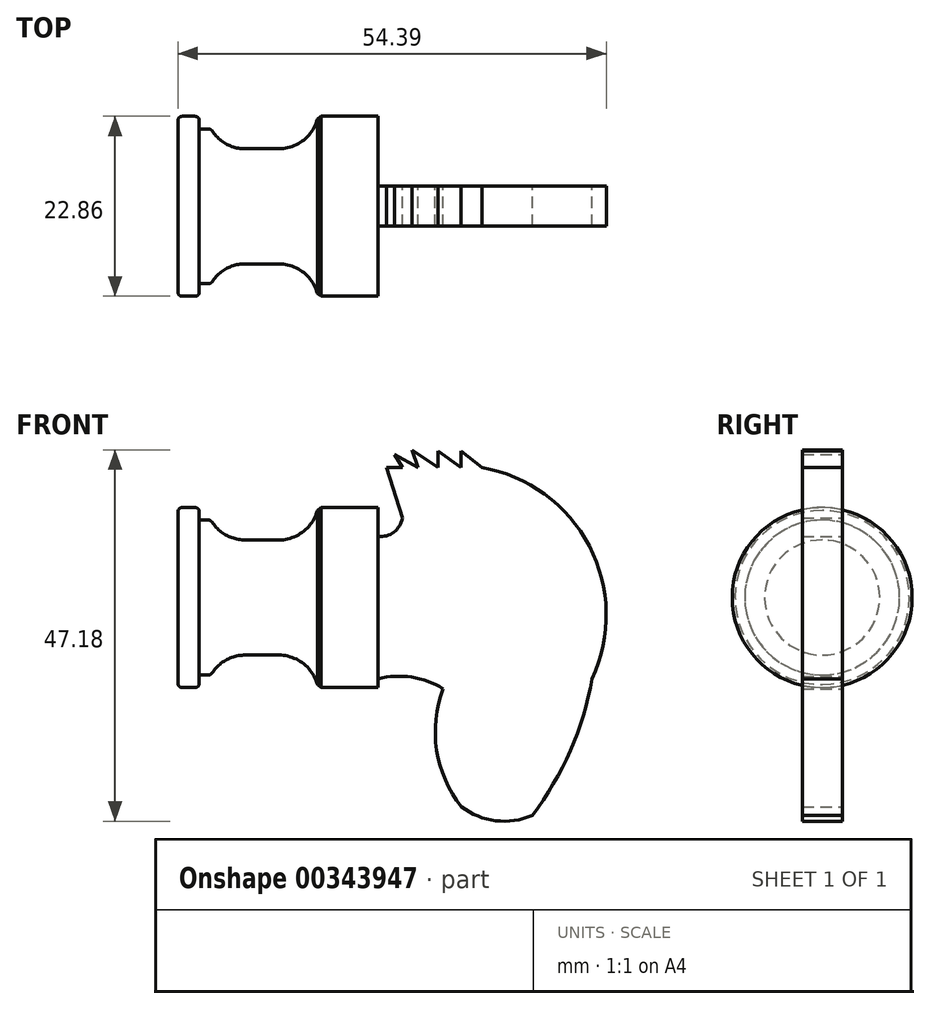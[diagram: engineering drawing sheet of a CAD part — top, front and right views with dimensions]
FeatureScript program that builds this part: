
annotation { "Feature Type Name" : "Feature", "Feature Type Description" : "" }
export const myFeature = defineFeature(function(context is Context, id is Id, definition is map)
    precondition{}
    {
        {
            var Q0;
            Q0=qCreatedBy(makeId("Front.planeOp"),FACE);
            var sketch = newSketch(context, id + "F0", { "sketchPlane" : qUnion([Q0])});
            skLineSegment(sketch, "E0", {"start": v(0, 0) * mm, "end": v(-25.4, 0) * mm});
            skLineSegment(sketch, "E1", {"start": v(-25.4, 0) * mm, "end": v(-25.4, 11.43) * mm});
            skLineSegment(sketch, "E2", {"start": v(-25.4, 11.43) * mm, "end": v(-22.71, 11.43) * mm});
            skLineSegment(sketch, "E3", {"start": v(-22.71, 11.43) * mm, "end": v(-22.71, 9.84) * mm});
            skLineSegment(sketch, "E4", {"start": v(-22.71, 9.84) * mm, "end": v(-21.25, 9.84) * mm});
            skLineSegment(sketch, "E5", {"start": v(-21.25, 9.84) * mm, "end": v(-20.32, 7.31) * mm});
            skLineSegment(sketch, "E6", {"start": v(-20.32, 7.31) * mm, "end": v(-7.62, 7.31) * mm});
            skLineSegment(sketch, "E7", {"start": v(-7.62, 7.31) * mm, "end": v(-7.62, 11.43) * mm});
            skLineSegment(sketch, "E8", {"start": v(-7.62, 11.43) * mm, "end": v(0, 11.43) * mm});
            skLineSegment(sketch, "E9", {"start": v(0, 11.43) * mm, "end": v(0, 0) * mm});
            skSolve(sketch);
        }
        {
            var Q0;
            Q0=makeQuery(id+"F0.imprint","IMPRINT",FACE,{"disambiguationData":[TD([[makeQuery(id+"F0.imprint","IMPRINT",EDGE,{"derivedFrom":sQuery(id+"F0.wireOp",EDGE,"E0")}),-1.0]])]});
            var Q1;
            Q1=sQuery(id+"F0.wireOp",EDGE,"E0");
            revolve(context, id + "F1", {"entities" : qUnion([Q0]), "axis" : qUnion([Q1]), "revolveType" : RevolveType.FULL});
        }
        {
            var Q0;
            Q0=makeQuery(id+"F1.opRevolve","SWEPT_EDGE",EDGE,{"disambiguationData":[OSD([sQuery(id+"F0.wireOp",EDGE,"E5"),sQuery(id+"F0.wireOp",EDGE,"E6")])]});
            fillet(context, id + "F2", {"entities" : qUnion([Q0]), "radius" : 5.08 * mm, "tangentPropagation" : true, "allowEdgeOverflow" : false});
        }
        {
            var Q0;
            Q0=makeQuery(id+"F1.opRevolve","SWEPT_EDGE",EDGE,{"disambiguationData":[OSD([sQuery(id+"F0.wireOp",EDGE,"E6"),sQuery(id+"F0.wireOp",EDGE,"E7")])]});
            fillet(context, id + "F3", {"entities" : qUnion([Q0]), "radius" : 5.08 * mm, "tangentPropagation" : true, "allowEdgeOverflow" : false});
        }
        {
            var Q0;
            Q0=makeQuery(id+"F2.opFillet","BLEND_EDGE",EDGE,{"blendedFrom":[makeQuery(id+"F1.opRevolve","SWEPT_EDGE",EDGE,{"disambiguationData":[OSD([sQuery(id+"F0.wireOp",EDGE,"E5"),sQuery(id+"F0.wireOp",EDGE,"E6")])]}),makeQuery(id+"F1.opRevolve","SWEPT_FACE",FACE,{"disambiguationData":[OSD([sQuery(id+"F0.wireOp",EDGE,"E4")])]})],"blendedInto":[makeQuery(id+"F1.opRevolve","SWEPT_FACE",FACE,{"disambiguationData":[OSD([sQuery(id+"F0.wireOp",EDGE,"E4")])]})]});
            var Q1;
            Q1=makeQuery(id+"F1.opRevolve","SWEPT_EDGE",EDGE,{"disambiguationData":[OSD([sQuery(id+"F0.wireOp",EDGE,"E2"),sQuery(id+"F0.wireOp",EDGE,"E3")])]});
            var Q2;
            Q2=makeQuery(id+"F1.opRevolve","SWEPT_EDGE",EDGE,{"disambiguationData":[OSD([sQuery(id+"F0.wireOp",EDGE,"E1"),sQuery(id+"F0.wireOp",EDGE,"E2")])]});
            fillet(context, id + "F4", {"entities" : qUnion([Q0, Q1, Q2]), "radius" : 0.5 * mm, "tangentPropagation" : true, "allowEdgeOverflow" : false});
        }
        {
            var Q0;
            {var subQ0=sQuery(id+"F0.wireOp",EDGE,"E9");var subQ1=sQuery(id+"F0.wireOp",EDGE,"E8");var subQ2=makeQuery(id+"F1.opRevolve","SWEPT_EDGE",EDGE,{"disambiguationData":[OSD([subQ1,subQ0])]});Q0=makeQuery(id+"F3.opFillet","BLEND_EDGE",EDGE,{"blendedFrom":[makeQuery(id+"F1.opRevolve","SWEPT_EDGE",EDGE,{"disambiguationData":[OSD([sQuery(id+"F0.wireOp",EDGE,"E6"),sQuery(id+"F0.wireOp",EDGE,"E7")])]}),makeQuery(id+"FKdUeLkxdvxAeGn_1.boolean.opBoolean","MERGE",FACE,{"derivedFrom":[makeQuery(id+"F1.opRevolve","SWEPT_FACE",FACE,{"disambiguationData":[OSD([subQ1])]}),makeQuery(id+"FKdUeLkxdvxAeGn_1.opExtrude","SWEPT_FACE",FACE,{"disambiguationData":[OSD([subQ1,subQ0]),TDD([makeQuery(id+"FhPrJ5y7E5olnpu_1.imprint","IMPRINT",EDGE,{"disambiguationData":[TD([[makeQuery(id+"FhPrJ5y7E5olnpu_1.imprint","INTERSECT",VERTEX,{"derivedFrom":[subQ2,sQuery(id+"FhPrJ5y7E5olnpu_1.wireOp",EDGE,"5swccAFu-Qq9y-H5FG-WLZN-0cyFNXjqbd3L")]}),1.0]])],"derivedFrom":subQ2})])]}),makeQuery(id+"FKdUeLkxdvxAeGn_1.opExtrude","SWEPT_FACE",FACE,{"disambiguationData":[OSD([subQ1,subQ0]),TDD([makeQuery(id+"FhPrJ5y7E5olnpu_1.imprint","IMPRINT",EDGE,{"disambiguationData":[TD([[makeQuery(id+"FhPrJ5y7E5olnpu_1.imprint","INTERSECT",VERTEX,{"derivedFrom":[subQ2,sQuery(id+"FhPrJ5y7E5olnpu_1.wireOp",EDGE,"yrlBlJsE-glzK-ckup-w4H4-O8etLDBYbZ2E")]}),1.0]])],"derivedFrom":subQ2})])]}),makeQuery(id+"FKdUeLkxdvxAeGn_1.opExtrude","SWEPT_FACE",FACE,{"disambiguationData":[OSD([subQ1,subQ0]),TDD([makeQuery(id+"FhPrJ5y7E5olnpu_1.imprint","IMPRINT",EDGE,{"disambiguationData":[TD([[makeQuery(id+"FhPrJ5y7E5olnpu_1.imprint","INTERSECT",VERTEX,{"derivedFrom":[subQ2,sQuery(id+"FhPrJ5y7E5olnpu_1.wireOp",EDGE,"59esLNOy-bGTi-q598-Dafd-GjDcgzXxW0rH")]}),-1.0]])],"derivedFrom":subQ2})])]}),makeQuery(id+"FKdUeLkxdvxAeGn_1.opExtrude","SWEPT_FACE",FACE,{"disambiguationData":[OSD([subQ1,subQ0]),TDD([makeQuery(id+"FhPrJ5y7E5olnpu_1.imprint","IMPRINT",EDGE,{"disambiguationData":[TD([[makeQuery(id+"FhPrJ5y7E5olnpu_1.imprint","INTERSECT",VERTEX,{"derivedFrom":[subQ2,sQuery(id+"FhPrJ5y7E5olnpu_1.wireOp",EDGE,"8v8Xe1NO-uW00-CEbA-Of9p-lGgIFj4n3XNv")]}),-1.0]])],"derivedFrom":subQ2})])]})]})],"blendedInto":[makeQuery(id+"FKdUeLkxdvxAeGn_1.boolean.opBoolean","MERGE",FACE,{"derivedFrom":[makeQuery(id+"F1.opRevolve","SWEPT_FACE",FACE,{"disambiguationData":[OSD([subQ1])]}),makeQuery(id+"FKdUeLkxdvxAeGn_1.opExtrude","SWEPT_FACE",FACE,{"disambiguationData":[OSD([subQ1,subQ0]),TDD([makeQuery(id+"FhPrJ5y7E5olnpu_1.imprint","IMPRINT",EDGE,{"disambiguationData":[TD([[makeQuery(id+"FhPrJ5y7E5olnpu_1.imprint","INTERSECT",VERTEX,{"derivedFrom":[subQ2,sQuery(id+"FhPrJ5y7E5olnpu_1.wireOp",EDGE,"5swccAFu-Qq9y-H5FG-WLZN-0cyFNXjqbd3L")]}),1.0]])],"derivedFrom":subQ2})])]}),makeQuery(id+"FKdUeLkxdvxAeGn_1.opExtrude","SWEPT_FACE",FACE,{"disambiguationData":[OSD([subQ1,subQ0]),TDD([makeQuery(id+"FhPrJ5y7E5olnpu_1.imprint","IMPRINT",EDGE,{"disambiguationData":[TD([[makeQuery(id+"FhPrJ5y7E5olnpu_1.imprint","INTERSECT",VERTEX,{"derivedFrom":[subQ2,sQuery(id+"FhPrJ5y7E5olnpu_1.wireOp",EDGE,"yrlBlJsE-glzK-ckup-w4H4-O8etLDBYbZ2E")]}),1.0]])],"derivedFrom":subQ2})])]}),makeQuery(id+"FKdUeLkxdvxAeGn_1.opExtrude","SWEPT_FACE",FACE,{"disambiguationData":[OSD([subQ1,subQ0]),TDD([makeQuery(id+"FhPrJ5y7E5olnpu_1.imprint","IMPRINT",EDGE,{"disambiguationData":[TD([[makeQuery(id+"FhPrJ5y7E5olnpu_1.imprint","INTERSECT",VERTEX,{"derivedFrom":[subQ2,sQuery(id+"FhPrJ5y7E5olnpu_1.wireOp",EDGE,"59esLNOy-bGTi-q598-Dafd-GjDcgzXxW0rH")]}),-1.0]])],"derivedFrom":subQ2})])]}),makeQuery(id+"FKdUeLkxdvxAeGn_1.opExtrude","SWEPT_FACE",FACE,{"disambiguationData":[OSD([subQ1,subQ0]),TDD([makeQuery(id+"FhPrJ5y7E5olnpu_1.imprint","IMPRINT",EDGE,{"disambiguationData":[TD([[makeQuery(id+"FhPrJ5y7E5olnpu_1.imprint","INTERSECT",VERTEX,{"derivedFrom":[subQ2,sQuery(id+"FhPrJ5y7E5olnpu_1.wireOp",EDGE,"8v8Xe1NO-uW00-CEbA-Of9p-lGgIFj4n3XNv")]}),-1.0]])],"derivedFrom":subQ2})])]})]})]});}
            chamfer(context, id + "F5", {"entities" : qUnion([Q0]), "width" : 0.5 * mm, "tangentPropagation" : true});
        }
        {
            var Q0;
            Q0=qCreatedBy(makeId("Front.planeOp"),FACE);
            var sketch = newSketch(context, id + "F6", { "sketchPlane" : qUnion([Q0])});
            skArc(sketch, "E10", {"start": v(0, 7.76) * mm, "mid": v(2, 8.32) * mm, "end": v(3.1, 10.1) * mm});
            skLineSegment(sketch, "E11", {"start": v(3.1, 10.1) * mm, "end": v(1.1, 16.51) * mm});
            skLineSegment(sketch, "E12", {"start": v(1.1, 16.51) * mm, "end": v(3.1, 16.51) * mm});
            skLineSegment(sketch, "E13", {"start": v(3.1, 16.51) * mm, "end": v(2.1, 18.18) * mm});
            skPoint(sketch, "E13.endSnap0", {"position": v(2.1, 16.51) * mm});
            skLineSegment(sketch, "E14", {"start": v(2.1, 18.18) * mm, "end": v(5.1, 16.51) * mm});
            skLineSegment(sketch, "E15", {"start": v(5.1, 16.51) * mm, "end": v(4.34, 18.77) * mm});
            skLineSegment(sketch, "E16", {"start": v(4.34, 18.77) * mm, "end": v(7.6, 16.51) * mm});
            skLineSegment(sketch, "E17", {"start": v(7.6, 16.51) * mm, "end": v(7.6, 18.6) * mm});
            skLineSegment(sketch, "E18", {"start": v(7.6, 18.6) * mm, "end": v(10.51, 16.51) * mm});
            skLineSegment(sketch, "E19", {"start": v(10.51, 16.51) * mm, "end": v(10.51, 18.6) * mm});
            skLineSegment(sketch, "E20", {"start": v(10.51, 18.6) * mm, "end": v(13.18, 16.51) * mm});
            skArc(sketch, "E21", {"start": v(27.19, -10.33) * mm, "mid": v(26.83, 6.56) * mm, "end": v(13.18, 16.51) * mm});
            skArc(sketch, "E22", {"start": v(19.6, -27.67) * mm, "mid": v(24.42, -19.45) * mm, "end": v(27.19, -10.33) * mm});
            skArc(sketch, "E23", {"start": v(10.6, -26.59) * mm, "mid": v(14.95, -28.35) * mm, "end": v(19.6, -27.67) * mm});
            skArc(sketch, "E24", {"start": v(8.26, -11.58) * mm, "mid": v(7.45, -19.4) * mm, "end": v(10.6, -26.59) * mm});
            skArc(sketch, "E25", {"start": v(8.26, -11.58) * mm, "mid": v(4.26, -10.12) * mm, "end": v(0, -10.33) * mm});
            skLineSegment(sketch, "E26", {"start": v(0, -10.33) * mm, "end": v(0, 7.76) * mm});
            skSolve(sketch);
        }
        {
            var Q0;
            Q0=makeQuery(id+"F6.imprint","IMPRINT",FACE,{"disambiguationData":[TD([[makeQuery(id+"F6.imprint","IMPRINT",EDGE,{"derivedFrom":sQuery(id+"F6.wireOp",EDGE,"E10")}),-1.0]])]});
            extrude(context, id + "F7", {"entities" : qUnion([Q0]), "operationType" : NewBodyOperationType.ADD, "endBound" : BoundingType.SYMMETRIC, "depth" : 5.08 * mm});
        }
    });
